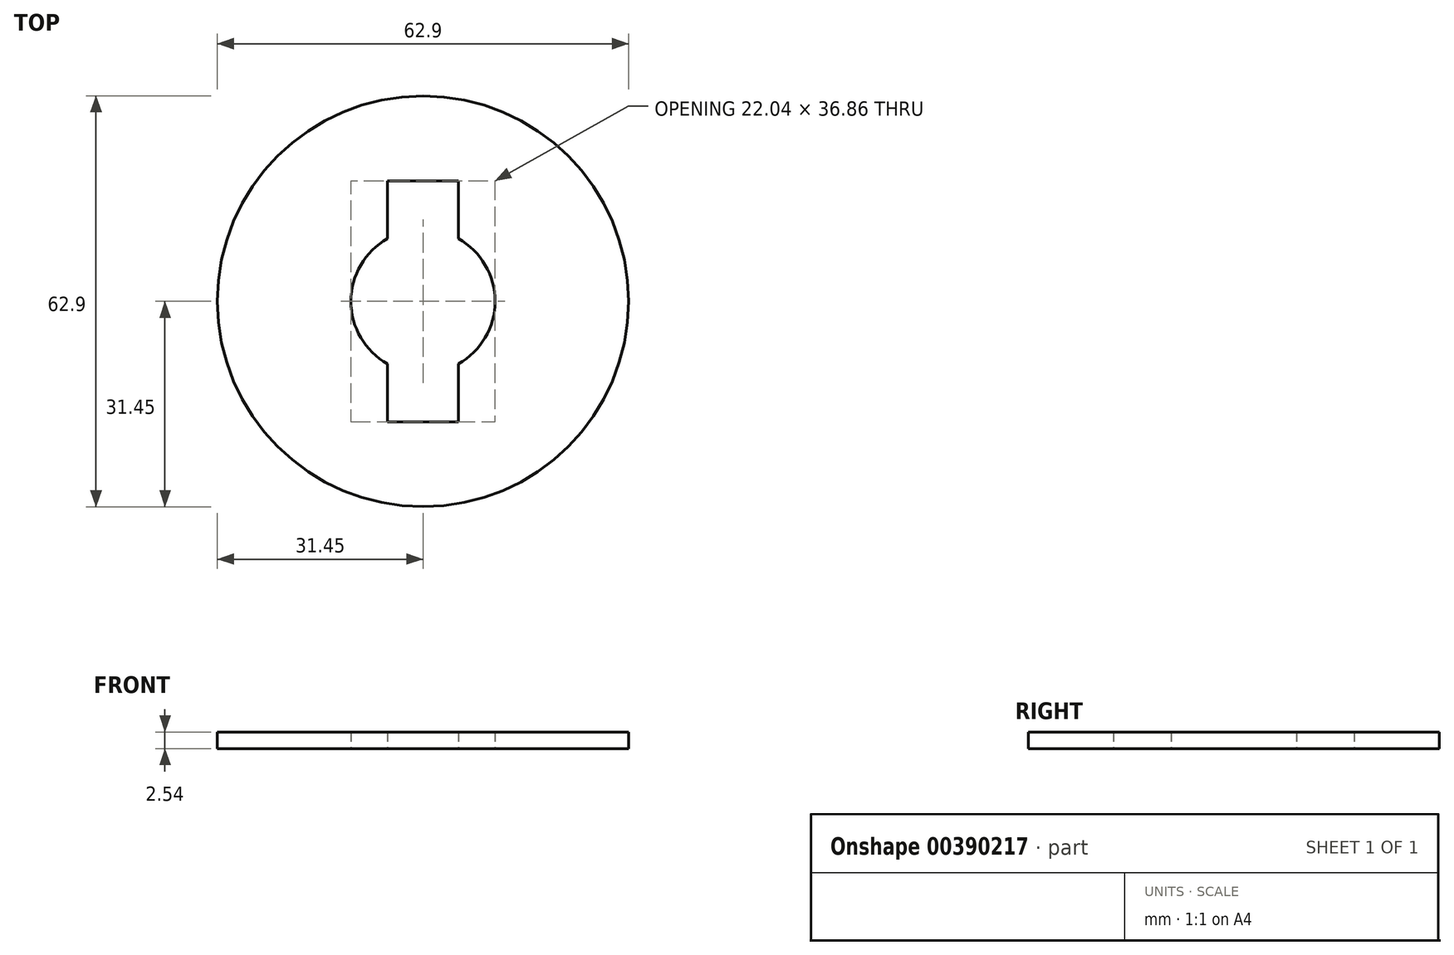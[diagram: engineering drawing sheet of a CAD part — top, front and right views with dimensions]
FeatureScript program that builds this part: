
annotation { "Feature Type Name" : "Feature", "Feature Type Description" : "" }
export const myFeature = defineFeature(function(context is Context, id is Id, definition is map)
    precondition{}
    {
        {
            var Q0;
            Q0=qCreatedBy(makeId("Top.planeOp"),FACE);
            var sketch = newSketch(context, id + "F0", { "sketchPlane" : qUnion([Q0])});
            skCircle(sketch, "E0", {"center": v(0, 0) * mm, "radius": 31.45 * mm});
            skCircle(sketch, "E1", {"center": v(0, 0) * mm, "radius": 11.02 * mm});
            skLineSegment(sketch, "E2.bottom", {"start": v(5.43, 18.43) * mm, "end": v(-5.43, 18.43) * mm});
            skLineSegment(sketch, "E2.top", {"start": v(5.43, -18.43) * mm, "end": v(-5.43, -18.43) * mm});
            skLineSegment(sketch, "E2.left", {"start": v(5.43, 18.43) * mm, "end": v(5.43, -18.43) * mm});
            skLineSegment(sketch, "E2.right", {"start": v(-5.43, 18.43) * mm, "end": v(-5.43, -18.43) * mm});
            skSolve(sketch);
        }
        {
            var Q0;
            Q0=qSketchRegion(id+"F0",true);
            extrude(context, id + "F1", {"entities" : qUnion([Q0]), "depth" : 2.54 * mm});
        }
    });
